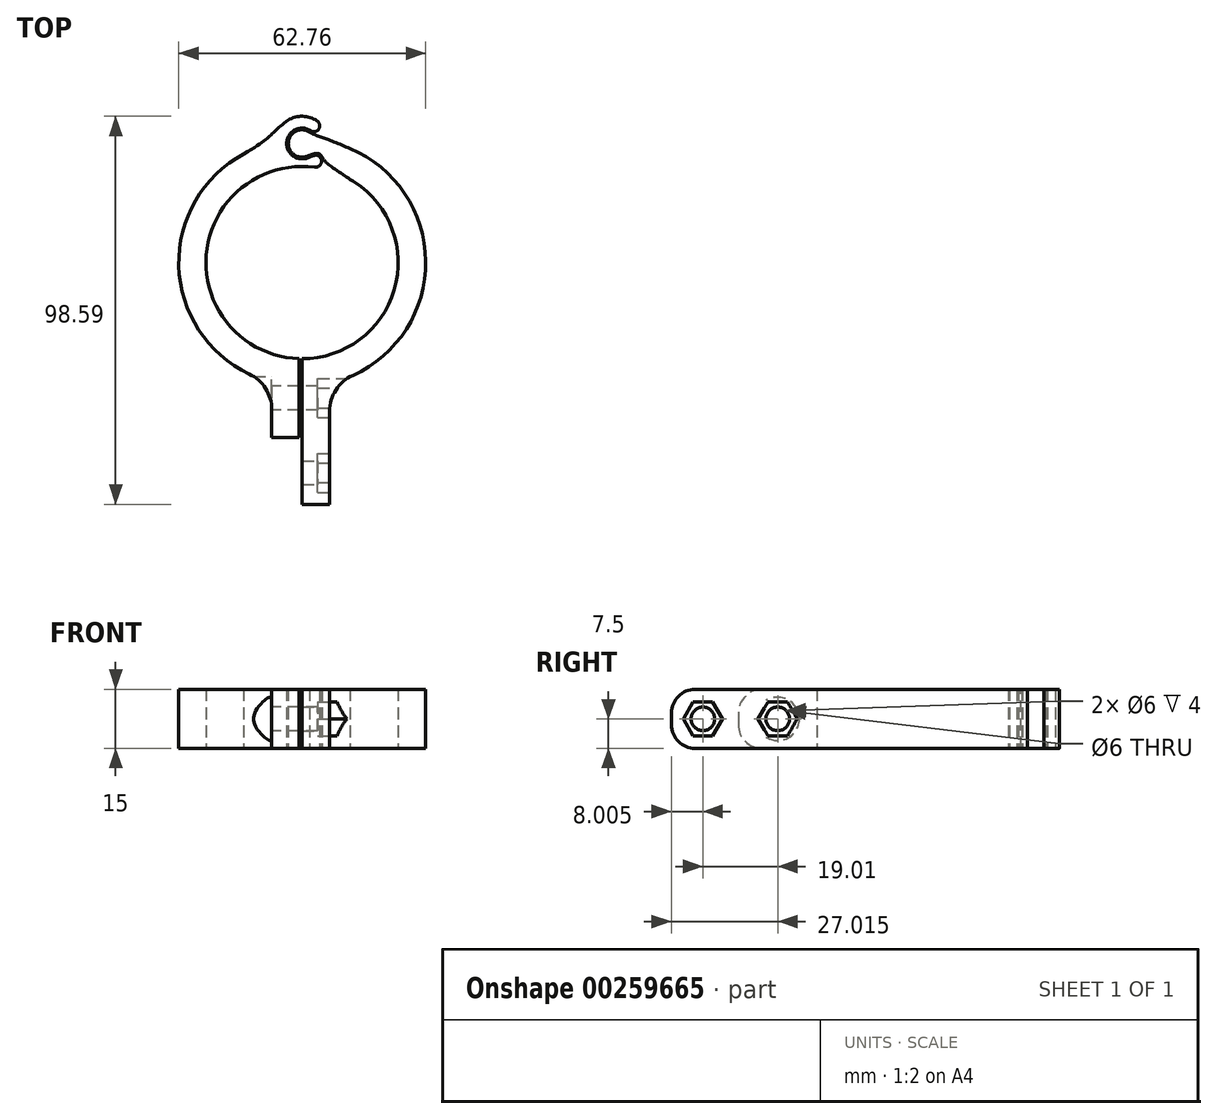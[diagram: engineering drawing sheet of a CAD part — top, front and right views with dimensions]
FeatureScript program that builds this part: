
annotation { "Feature Type Name" : "Feature", "Feature Type Description" : "" }
export const myFeature = defineFeature(function(context is Context, id is Id, definition is map)
    precondition{}
    {
        {
            var Q0;
            Q0=qCreatedBy(makeId("Top.planeOp"),FACE);
            var sketch = newSketch(context, id + "F0", { "sketchPlane" : qUnion([Q0])});
            skArc(sketch, "E0", {"start": v(7, -30.64) * mm, "mid": v(31.3, -2.72) * mm, "end": v(12.18, 28.97) * mm});
            skArc(sketch, "E1", {"start": v(0, -24.43) * mm, "mid": v(23.42, -6.94) * mm, "end": v(13.32, 20.48) * mm});
            skLineSegment(sketch, "E2.top", {"start": v(0, -61.42) * mm, "end": v(7, -61.42) * mm});
            skLineSegment(sketch, "E2.left", {"start": v(0, -35) * mm, "end": v(0, -61.42) * mm});
            skLineSegment(sketch, "E2.right", {"start": v(7, -30.64) * mm, "end": v(7, -61.42) * mm});
            skLineSegment(sketch, "E3.top", {"start": v(-0.7, -44.41) * mm, "end": v(-7.7, -44.41) * mm});
            skLineSegment(sketch, "E3.right", {"start": v(-7.7, -30.36) * mm, "end": v(-7.7, -44.41) * mm});
            skPoint(sketch, "E2.bottom.start.orphan", {"position": v(0, -24.43) * mm});
            skLineSegment(sketch, "E4", {"start": v(0, -35) * mm, "end": v(0, -24.43) * mm});
            skLineSegment(sketch, "E5", {"start": v(-0.7, -44.41) * mm, "end": v(-0.7, -24.41) * mm});
            skArc(sketch, "E6", {"start": v(1.96, 33.16) * mm, "mid": v(-3.49, 30.54) * mm, "end": v(1.45, 27.07) * mm});
            skArc(sketch, "E7", {"start": v(3.15, 24.22) * mm, "mid": v(4.67, 24.9) * mm, "end": v(4.76, 26.56) * mm});
            skFitSpline(sketch, "E8", {"points": [v(1.62, 26.71) * mm, v(2.82, 27.14) * mm, v(4.76, 26.56) * mm], "startDerivative": vector(6.48, 2.96) * mm, "endDerivative": vector(3.23, -6.01) * mm});
            skArc(sketch, "E9.0", {"start": v(-3.8, 31.1) * mm, "mid": v(-2.45, 27.22) * mm, "end": v(1.62, 26.71) * mm});
            skFitSpline(sketch, "E10.0", {"points": [v(1.45, 27.07) * mm, v(1.73, 27.2) * mm, v(2.02, 27.32) * mm, v(2.27, 27.42) * mm, v(2.42, 27.46) * mm, v(2.54, 27.49) * mm, v(2.61, 27.5) * mm, v(2.67, 27.52) * mm, v(2.75, 27.54) * mm, v(2.86, 27.58) * mm, v(3.03, 27.63) * mm, v(3.27, 27.69) * mm, v(3.56, 27.72) * mm, v(3.88, 27.71) * mm, v(4.22, 27.62) * mm, v(4.56, 27.44) * mm, v(4.86, 27.15) * mm, v(5.04, 26.9) * mm, v(5.11, 26.75) * mm]});
            skArc(sketch, "E11", {"start": v(2.16, 33.5) * mm, "mid": v(4.24, 33.93) * mm, "end": v(3.81, 36) * mm});
            skFitSpline(sketch, "E12", {"points": [v(1.96, 33.16) * mm, v(7.12, 31.06) * mm, v(13.92, 28.17) * mm], "startDerivative": vector(12.67, -7.81) * mm, "endDerivative": vector(8.16, -3.78) * mm});
            skFitSpline(sketch, "E13", {"points": [v(5.09, 26.8) * mm, v(6.88, 24.8) * mm, v(13.32, 20.48) * mm], "startDerivative": vector(3.33, -5.17) * mm, "endDerivative": vector(6.27, -4.08) * mm});
            skArc(sketch, "E14.trimOffspring", {"start": v(3.15, 24.22) * mm, "mid": v(-24.35, 1.93) * mm, "end": v(-0.7, -24.41) * mm});
            skArc(sketch, "E15.trimOffspring", {"start": v(-14.87, 27.57) * mm, "mid": v(-31.09, -3.85) * mm, "end": v(-7.7, -30.36) * mm});
            skArc(sketch, "E16.0", {"start": v(3.81, 36) * mm, "mid": v(0.15, 37.16) * mm, "end": v(-3.56, 36.17) * mm});
            skFitSpline(sketch, "E17", {"points": [v(-3.56, 36.17) * mm, v(-7.6, 32.7) * mm, v(-16.9, 26.38) * mm], "startDerivative": vector(-12.87, -9.12) * mm, "endDerivative": vector(-32.57, -18.97) * mm});
            skArc(sketch, "E18.0", {"start": v(2.16, 33.5) * mm, "mid": v(-1.46, 33.87) * mm, "end": v(-3.8, 31.1) * mm});
            skSolve(sketch);
        }
        {
            var Q0;
            Q0 = qSketchRegion(id + "F0", true);
            extrude(context, id + "F1", {"entities" : qUnion([Q0]), "depth" : 15 * mm});
        }
        {
            var Q0;
            Q0=makeQuery(id+"F1.opExtrude","CAP_EDGE",EDGE,{"disambiguationData":[OSD([sQuery(id+"F0.wireOp",EDGE,"E3.top")])],"isStart":false});
            var Q1;
            Q1=makeQuery(id+"F1.opExtrude","CAP_EDGE",EDGE,{"disambiguationData":[OSD([sQuery(id+"F0.wireOp",EDGE,"E2.top")])],"isStart":false});
            var Q2;
            Q2=makeQuery(id+"F1.opExtrude","CAP_EDGE",EDGE,{"disambiguationData":[OSD([sQuery(id+"F0.wireOp",EDGE,"E3.top")])],"isStart":true});
            var Q3;
            Q3=makeQuery(id+"F1.opExtrude","CAP_EDGE",EDGE,{"disambiguationData":[OSD([sQuery(id+"F0.wireOp",EDGE,"E2.top")])],"isStart":true});
            fillet(context, id + "F2", {"entities" : qUnion([Q0, Q1, Q2, Q3]), "radius" : 6 * mm, "tangentPropagation" : true, "allowEdgeOverflow" : false});
        }
        {
            var Q0;
            Q0=makeQuery(id+"F1.opExtrude","SWEPT_EDGE",EDGE,{"disambiguationData":[OSD([sQuery(id+"F0.wireOp",EDGE,"E0"),sQuery(id+"F0.wireOp",EDGE,"E2.right")])]});
            var Q1;
            Q1=makeQuery(id+"F1.opExtrude","SWEPT_EDGE",EDGE,{"disambiguationData":[OSD([sQuery(id+"F0.wireOp",EDGE,"E3.right"),sQuery(id+"F0.wireOp",EDGE,"E15.trimOffspring")])]});
            fillet(context, id + "F3", {"entities" : qUnion([Q0, Q1]), "radius" : 10 * mm, "tangentPropagation" : true, "allowEdgeOverflow" : false});
        }
        {
            var Q0;
            Q0=makeQuery(id+"F1.opExtrude","SWEPT_FACE",FACE,{"disambiguationData":[OSD([sQuery(id+"F0.wireOp",EDGE,"E3.left"),sQuery(id+"F0.wireOp",EDGE,"E5")])]});
            var Q1;
            {var subQ0=sQuery(id+"F0.wireOp",EDGE,"E3.right");var subQ1=sQuery(id+"F0.wireOp",EDGE,"E15.trimOffspring");Q1=makeQuery(id+"F3.opFillet","BLEND_VERTEX",VERTEX,{"blendedFrom":[makeQuery(id+"F1.opExtrude","SWEPT_EDGE",EDGE,{"disambiguationData":[OSD([subQ0,subQ1])]}),makeQuery(id+"F1.opExtrude","CAP_FACE",FACE,{"disambiguationData":[OSD([sQuery(id+"F0.wireOp",EDGE,"E3.top"),sQuery(id+"F0.wireOp",EDGE,"E3.left"),subQ0,sQuery(id+"F0.wireOp",EDGE,"E5"),sQuery(id+"F0.wireOp",EDGE,"E7"),sQuery(id+"F0.wireOp",EDGE,"E8"),sQuery(id+"F0.wireOp",EDGE,"E9.0"),sQuery(id+"F0.wireOp",EDGE,"E11"),sQuery(id+"F0.wireOp",EDGE,"E14.trimOffspring"),subQ1,sQuery(id+"F0.wireOp",EDGE,"E16.0"),sQuery(id+"F0.wireOp",EDGE,"E17"),sQuery(id+"F0.wireOp",EDGE,"E18.0")])],"isStart":false}),makeQuery(id+"F1.opExtrude","SWEPT_FACE",FACE,{"disambiguationData":[OSD([subQ0])]})],"blendedInto":[makeQuery(id+"F1.opExtrude","CAP_FACE",FACE,{"disambiguationData":[OSD([sQuery(id+"F0.wireOp",EDGE,"E3.top"),sQuery(id+"F0.wireOp",EDGE,"E3.left"),subQ0,sQuery(id+"F0.wireOp",EDGE,"E5"),sQuery(id+"F0.wireOp",EDGE,"E7"),sQuery(id+"F0.wireOp",EDGE,"E8"),sQuery(id+"F0.wireOp",EDGE,"E9.0"),sQuery(id+"F0.wireOp",EDGE,"E11"),sQuery(id+"F0.wireOp",EDGE,"E14.trimOffspring"),subQ1,sQuery(id+"F0.wireOp",EDGE,"E16.0"),sQuery(id+"F0.wireOp",EDGE,"E17"),sQuery(id+"F0.wireOp",EDGE,"E18.0")])],"isStart":false}),makeQuery(id+"F1.opExtrude","SWEPT_FACE",FACE,{"disambiguationData":[OSD([subQ0])]})]});}
            cPlane(context, id + "F4", {"entities" : qUnion([Q0, Q1]), "cplaneType" : CPlaneType.PLANE_POINT, "offset" : 25 * mm, "width" : 150 * mm, "height" : 150 * mm});
        }
        {
            var Q0;
            Q0=qCreatedBy(id+"F4.planeOp",FACE);
            var sketch = newSketch(context, id + "F5", { "sketchPlane" : qUnion([Q0])});
            skCircle(sketch, "E19", {"center": v(-34.41, 7.5) * mm, "radius": 5.5 * mm});
            skSolve(sketch);
        }
        {
            var Q0;
            Q0 = qSketchRegion(id + "F5", true);
            extrude(context, id + "F6", {"entities" : qUnion([Q0]), "operationType" : NewBodyOperationType.REMOVE, "oppositeDirection" : true, "depth" : 25 * mm});
        }
        {
            var Q0;
            Q0=makeQuery(id+"F6.boolean.opBoolean","MERGE",FACE,{"derivedFrom":[makeQuery(id+"F1.opExtrude","SWEPT_FACE",FACE,{"disambiguationData":[OSD([sQuery(id+"F0.wireOp",EDGE,"E3.right")])]}),makeQuery(id+"F6.opExtrude","CAP_FACE",FACE,{"disambiguationData":[OSD([sQuery(id+"F5.wireOp",EDGE,"E19")])],"isStart":true})]});
            var sketch = newSketch(context, id + "F7", { "sketchPlane" : qUnion([Q0])});
            skCircle(sketch, "E20", {"center": v(34.41, 7.5) * mm, "radius": 3 * mm});
            skSolve(sketch);
        }
        {
            var Q0;
            Q0 = qSketchRegion(id + "F7", true);
            extrude(context, id + "F8", {"entities" : qUnion([Q0]), "operationType" : NewBodyOperationType.REMOVE, "oppositeDirection" : true, "depth" : 25 * mm});
        }
        {
            var Q0;
            Q0=makeQuery(id+"F1.opExtrude","SWEPT_FACE",FACE,{"disambiguationData":[OSD([sQuery(id+"F0.wireOp",EDGE,"E2.right")])]});
            var Q1;
            {var subQ0=sQuery(id+"F0.wireOp",EDGE,"E2.right");var subQ1=sQuery(id+"F0.wireOp",EDGE,"E2.top");Q1=makeQuery(id+"F2.opFillet","BLEND_VERTEX",VERTEX,{"blendedFrom":[makeQuery(id+"F1.opExtrude","CAP_EDGE",EDGE,{"disambiguationData":[OSD([subQ1])],"isStart":false}),makeQuery(id+"F1.opExtrude","CAP_FACE",FACE,{"disambiguationData":[OSD([sQuery(id+"F0.wireOp",EDGE,"E0"),sQuery(id+"F0.wireOp",EDGE,"E1"),subQ1,sQuery(id+"F0.wireOp",EDGE,"E2.left"),subQ0,sQuery(id+"F0.wireOp",EDGE,"E4"),sQuery(id+"F0.wireOp",EDGE,"E6"),sQuery(id+"F0.wireOp",EDGE,"E10.0"),sQuery(id+"F0.wireOp",EDGE,"E12"),sQuery(id+"F0.wireOp",EDGE,"E13")])],"isStart":false}),makeQuery(id+"F1.opExtrude","SWEPT_FACE",FACE,{"disambiguationData":[OSD([subQ0])]})],"blendedInto":[makeQuery(id+"F1.opExtrude","CAP_FACE",FACE,{"disambiguationData":[OSD([sQuery(id+"F0.wireOp",EDGE,"E0"),sQuery(id+"F0.wireOp",EDGE,"E1"),subQ1,sQuery(id+"F0.wireOp",EDGE,"E2.left"),subQ0,sQuery(id+"F0.wireOp",EDGE,"E4"),sQuery(id+"F0.wireOp",EDGE,"E6"),sQuery(id+"F0.wireOp",EDGE,"E10.0"),sQuery(id+"F0.wireOp",EDGE,"E12"),sQuery(id+"F0.wireOp",EDGE,"E13")])],"isStart":false}),makeQuery(id+"F1.opExtrude","SWEPT_FACE",FACE,{"disambiguationData":[OSD([subQ0])]})]});}
            cPlane(context, id + "F9", {"entities" : qUnion([Q0, Q1]), "cplaneType" : CPlaneType.PLANE_POINT, "offset" : 25 * mm, "width" : 150 * mm, "height" : 150 * mm});
        }
        {
            var Q0;
            Q0=qCreatedBy(id+"F9.planeOp",FACE);
            var sketch = newSketch(context, id + "F10", { "sketchPlane" : qUnion([Q0])});
            skCircle(sketch, "E21.cCircle", {"center": v(-34.41, 7.5) * mm, "radius": 4.3 * mm, "construction": true});
            skLineSegment(sketch, "E21.0", {"start": v(-31.93, 11.8) * mm, "end": v(-29.45, 7.5) * mm});
            skLineSegment(sketch, "E21.1", {"start": v(-29.45, 7.5) * mm, "end": v(-31.93, 3.2) * mm});
            skLineSegment(sketch, "E21.2", {"start": v(-31.93, 3.2) * mm, "end": v(-36.9, 3.2) * mm});
            skLineSegment(sketch, "E21.3", {"start": v(-36.9, 3.2) * mm, "end": v(-39.38, 7.5) * mm});
            skLineSegment(sketch, "E21.4", {"start": v(-39.38, 7.5) * mm, "end": v(-36.9, 11.8) * mm});
            skLineSegment(sketch, "E21.5", {"start": v(-36.9, 11.8) * mm, "end": v(-31.93, 11.8) * mm});
            skPoint(sketch, "E21.0.midPoint", {"position": v(-30.7, 9.65) * mm});
            skCircle(sketch, "E22.cCircle", {"center": v(-53.42, 7.5) * mm, "radius": 4.3 * mm, "construction": true});
            skLineSegment(sketch, "E22.0", {"start": v(-50.94, 11.8) * mm, "end": v(-48.46, 7.5) * mm});
            skLineSegment(sketch, "E22.1", {"start": v(-48.46, 7.5) * mm, "end": v(-50.94, 3.2) * mm});
            skLineSegment(sketch, "E22.2", {"start": v(-50.94, 3.2) * mm, "end": v(-55.9, 3.2) * mm});
            skLineSegment(sketch, "E22.3", {"start": v(-55.9, 3.2) * mm, "end": v(-58.4, 7.5) * mm});
            skLineSegment(sketch, "E22.4", {"start": v(-58.4, 7.5) * mm, "end": v(-55.9, 11.8) * mm});
            skLineSegment(sketch, "E22.5", {"start": v(-55.9, 11.8) * mm, "end": v(-50.94, 11.8) * mm});
            skPoint(sketch, "E22.0.midPoint", {"position": v(-49.7, 9.65) * mm});
            skSolve(sketch);
        }
        {
            var Q0;
            Q0 = qSketchRegion(id + "F10", true);
            extrude(context, id + "F11", {"entities" : qUnion([Q0]), "operationType" : NewBodyOperationType.REMOVE, "oppositeDirection" : true, "depth" : 3 * mm, "hasSecondDirection" : true, "secondDirectionOppositeDirection" : false, "secondDirectionDepth" : 25 * mm});
        }
        {
            var Q0;
            Q0=qCreatedBy(id+"F9.planeOp",FACE);
            var sketch = newSketch(context, id + "F12", { "sketchPlane" : qUnion([Q0])});
            skCircle(sketch, "E23", {"center": v(-53.42, 7.5) * mm, "radius": 3 * mm});
            skSolve(sketch);
        }
        {
            var Q0;
            Q0 = qSketchRegion(id + "F12", true);
            extrude(context, id + "F13", {"entities" : qUnion([Q0]), "operationType" : NewBodyOperationType.REMOVE, "endBound" : BoundingType.THROUGH_ALL, "oppositeDirection" : true, "depth" : 25 * mm});
        }
    });
